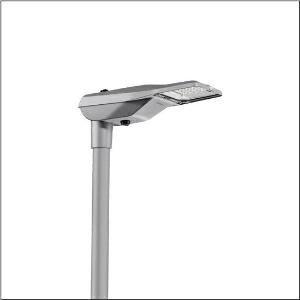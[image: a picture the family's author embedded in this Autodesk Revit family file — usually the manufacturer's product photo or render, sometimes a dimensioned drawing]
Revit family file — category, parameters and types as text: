
# Revit family: streetlight_sl_21_micro___st1_0ab_5xe1m33t08db_25ba
name_source: partatom
category: Lighting Fixtures
units: mm (PartAtom-declared; Revit-internal decimal feet)

## family parameters
Cut with Voids When Loaded = No
Host = Face
Light Source = No
Part Type = Normal
Room Calculation Point = No
Round Connector Dimension = Use Diameter
Shared = No

## types (1)
- --- (1 x LED, 4500 lm, 39.1 W, 3000K)
    Apparent Load = 39 VA
    CIE Flux Codes = 38 73 97 100 100
    Color Rendering = 70
    Color Temperature = 3000K
    Default Elevation = 1800 mm
    Description = Streetlight SL 21 micro, mast luminaire, primary light control with lens, of PMMA, primary optical cover: cover, of toughened safety glass, transparent, light distribution: ST1.0aB, light emission: direct distribution, primary light characteristic: asymmetric, installation type: side-entry, post-top, LED, High Power LED, rated luminous flux: 4.500lm, luminous efficacy: 115lm/W, light colour: 730, colour temperature: 3000K, control: flexible luminous flux parameterisation, time-dependent luminous flux control, constant luminous flux control, overheat protection, pre-setting: logarithmic dimming characteristic, mains connection: 220..240V, AC, 50/60Hz, start of lifetime: 39W, end of service life: 41W, reduction: 18W, luminaire housing, of diecast aluminium, powder-coated, Siteco® metallic grey (DB 702S), corrosivity category C5 mid according to DIN EN ISO 12944, please order mast flange separately, inclination adjustable: 0°, 5°, 10°, 15°, sealing non-destructively replaceable, multi-level sealing system, length: 528mm, width: 235mm, height: 110mm, mast flange for spigot size: 42mm (side-entry): 5XC10008XM4, 60/48mm (side-entry/post-top): 5XC10108XM2, 76/60mm (side-entry/post-top): 5XC10108XM1, Smart Interface below and above, protection rating (complete): IP66, insulation class (complete): insulation class II (safety insulation), certification: CE, ENEC, ENEC+, VDE, impact resistance: IK09, permissible operating ambient temperature for outdoor applications: -40..+50°C, standard-compliant lighting for roads and squares, packaging unit: 1 piece

Light Distribution: ST1.0aB
    Height = 110 mm
    Lamp = 1 x LED
    Lamp Light Flux = 4500 lm
    Lamp Power = 39.1 W
    Lamp count = 1
    Length = 528 mm
    Luminous efficacy = 115 lm/W
    Manufacturer = Siteco
    ModVariant = No
    Model = 5XE1M33T08DB
    Number of Poles = 1
    OnlyDefault = Yes
    Power Factor = 1
    Product Name = Streetlight SL 21 micro | ST1.0aB
    Product group = mast luminaire | pylon top
    ProductGroupID = 6100
    Protection Class = Protection class II
    Protection Degree = IP 66
    RLX_Detail_Level = 1
    RLX_Emergency_Light_Flux = 0 lm
    RLX_Emergency_Type = 0
    RLX_Emergency_Type_DB = No
    RlxData = <blob elided: 98141 chars, md5=44fb5a9c>
    Socket = socket
    Standby Power = 0 W
    System Light Flux = 4500 lm
    System Power = 39 W
    Type Comments = factory setting: luminous flux: 100 % | dim-lin: 254 | 765 mA
    Type Image = l_1007239.jpg
    URL = http://relux.com
    VarID = @adj_124311
    Voltage = 0 V
    Weight = 0.00 kg
    Width = 235 mm

## geometry (parser evidence)
native form markers: Blend x4, Sweep x9
no freeform markers — native parametric forms only
